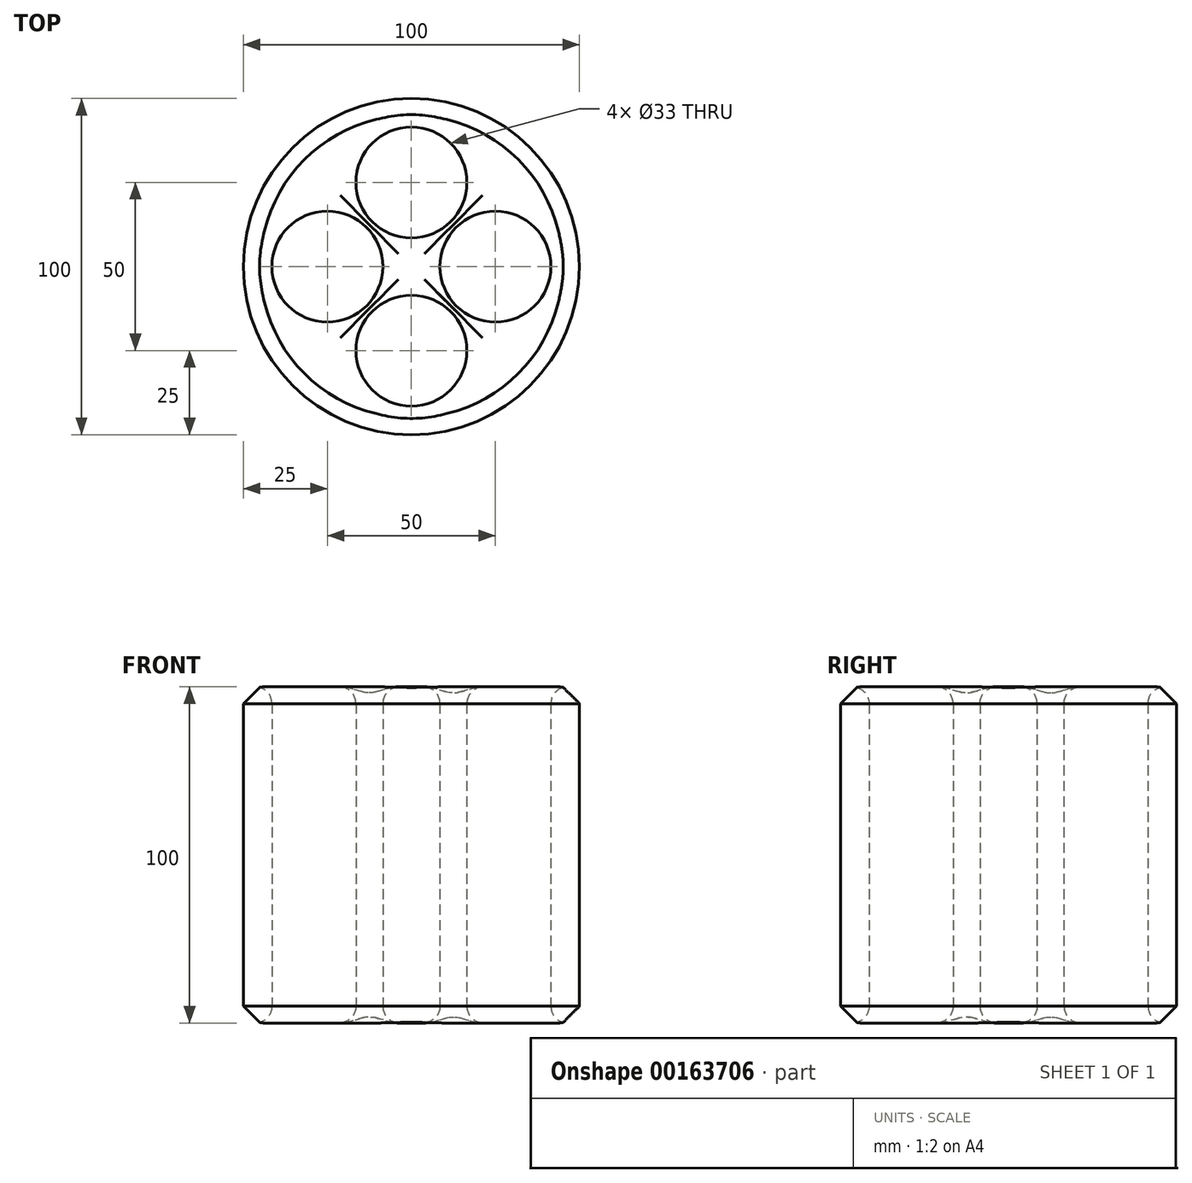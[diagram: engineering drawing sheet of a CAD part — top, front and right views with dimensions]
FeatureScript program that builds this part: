
annotation { "Feature Type Name" : "Feature", "Feature Type Description" : "" }
export const myFeature = defineFeature(function(context is Context, id is Id, definition is map)
    precondition{}
    {
        {
            var Q0;
            Q0=qCreatedBy(makeId("Top.planeOp"),FACE);
            var sketch = newSketch(context, id + "F0", { "sketchPlane" : qUnion([Q0])});
            skCircle(sketch, "E0", {"center": v(0, 0) * mm, "radius": 50 * mm});
            skCircle(sketch, "E1", {"center": v(25, 0) * mm, "radius": 16.5 * mm});
            skCircle(sketch, "E2", {"center": v(0, 25) * mm, "radius": 16.5 * mm});
            skCircle(sketch, "E3", {"center": v(-25, 0) * mm, "radius": 16.5 * mm});
            skCircle(sketch, "E4", {"center": v(0, -25) * mm, "radius": 16.5 * mm});
            skSolve(sketch);
        }
        {
            var Q0;
            Q0=makeQuery(id+"F0.imprint","IMPRINT",FACE,{"disambiguationData":[TD([[makeQuery(id+"F0.imprint","IMPRINT",EDGE,{"derivedFrom":sQuery(id+"F0.wireOp",EDGE,"E0")}),1.0]])]});
            extrude(context, id + "F1", {"entities" : qUnion([Q0]), "depth" : 100 * mm});
        }
        {
            var Q0;
            Q0=makeQuery(id+"F1.opExtrude","CAP_EDGE",EDGE,{"disambiguationData":[OSD([sQuery(id+"F0.wireOp",EDGE,"E1")])],"isStart":false});
            var Q1;
            Q1=makeQuery(id+"F1.opExtrude","CAP_EDGE",EDGE,{"disambiguationData":[OSD([sQuery(id+"F0.wireOp",EDGE,"E2")])],"isStart":false});
            var Q2;
            Q2=makeQuery(id+"F1.opExtrude","CAP_EDGE",EDGE,{"disambiguationData":[OSD([sQuery(id+"F0.wireOp",EDGE,"E3")])],"isStart":false});
            var Q3;
            Q3=makeQuery(id+"F1.opExtrude","CAP_EDGE",EDGE,{"disambiguationData":[OSD([sQuery(id+"F0.wireOp",EDGE,"E4")])],"isStart":false});
            fillet(context, id + "F2", {"entities" : qUnion([Q0, Q1, Q2, Q3]), "radius" : 5 * mm, "tangentPropagation" : true, "allowEdgeOverflow" : false});
        }
        {
            var Q0;
            Q0=makeQuery(id+"F1.opExtrude","CAP_EDGE",EDGE,{"disambiguationData":[OSD([sQuery(id+"F0.wireOp",EDGE,"E0")])],"isStart":false});
            chamfer(context, id + "F3", {"entities" : qUnion([Q0]), "width" : 5 * mm, "tangentPropagation" : true});
        }
        {
            var Q0;
            Q0=makeQuery(id+"F1.opExtrude","CAP_EDGE",EDGE,{"disambiguationData":[OSD([sQuery(id+"F0.wireOp",EDGE,"E0")])],"isStart":true});
            chamfer(context, id + "F4", {"entities" : qUnion([Q0]), "width" : 5 * mm, "tangentPropagation" : true});
        }
        {
            var Q0;
            Q0=makeQuery(id+"F1.opExtrude","CAP_EDGE",EDGE,{"disambiguationData":[OSD([sQuery(id+"F0.wireOp",EDGE,"E3")])],"isStart":true});
            var Q1;
            Q1=makeQuery(id+"F1.opExtrude","CAP_EDGE",EDGE,{"disambiguationData":[OSD([sQuery(id+"F0.wireOp",EDGE,"E2")])],"isStart":true});
            var Q2;
            Q2=makeQuery(id+"F1.opExtrude","CAP_EDGE",EDGE,{"disambiguationData":[OSD([sQuery(id+"F0.wireOp",EDGE,"E1")])],"isStart":true});
            var Q3;
            Q3=makeQuery(id+"F1.opExtrude","CAP_EDGE",EDGE,{"disambiguationData":[OSD([sQuery(id+"F0.wireOp",EDGE,"E4")])],"isStart":true});
            fillet(context, id + "F5", {"entities" : qUnion([Q0, Q1, Q2, Q3]), "radius" : 5 * mm, "tangentPropagation" : true, "allowEdgeOverflow" : false});
        }
    });
